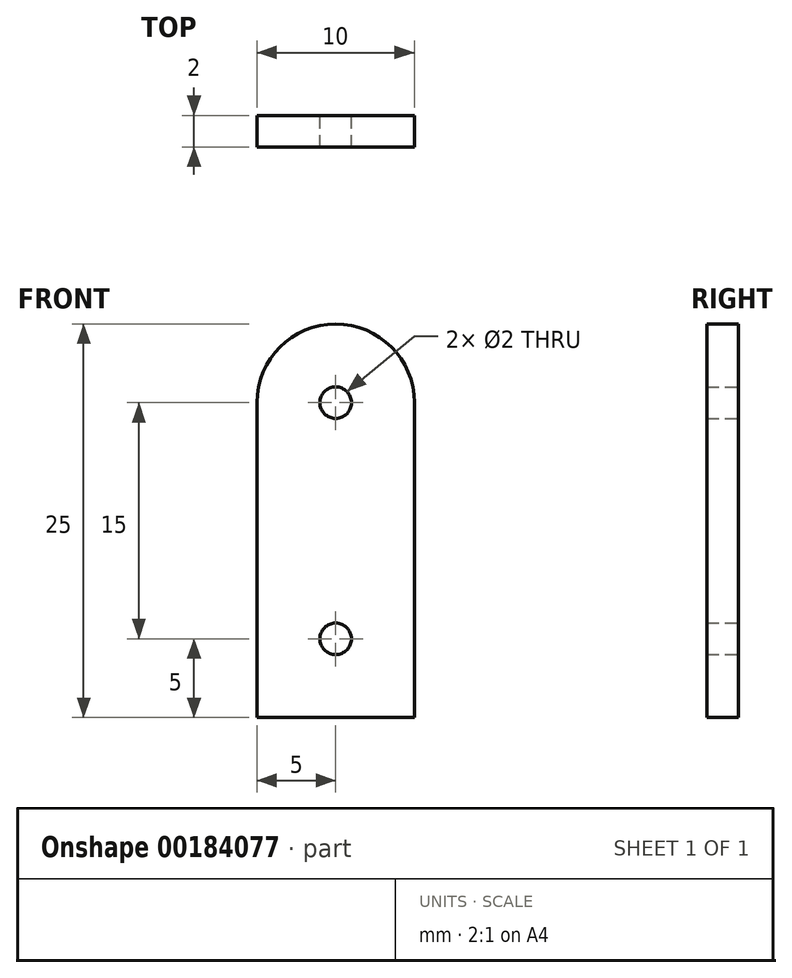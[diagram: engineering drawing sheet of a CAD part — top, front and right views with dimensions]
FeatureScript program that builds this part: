
annotation { "Feature Type Name" : "Feature", "Feature Type Description" : "" }
export const myFeature = defineFeature(function(context is Context, id is Id, definition is map)
    precondition{}
    {
        {
            var Q0;
            Q0=qCreatedBy(makeId("Front.planeOp"),FACE);
            var sketch = newSketch(context, id + "F0", { "sketchPlane" : qUnion([Q0])});
            skLineSegment(sketch, "E0.bottom", {"start": v(0, 0) * mm, "end": v(10, 0) * mm});
            skLineSegment(sketch, "E0.left", {"start": v(0, 0) * mm, "end": v(0, 20) * mm});
            skLineSegment(sketch, "E0.right", {"start": v(10, 0) * mm, "end": v(10, 20) * mm});
            skArc(sketch, "E1", {"start": v(10, 20) * mm, "mid": v(5, 25) * mm, "end": v(0, 20) * mm});
            skCircle(sketch, "E2", {"center": v(5, 20) * mm, "radius": 1 * mm});
            skCircle(sketch, "E3", {"center": v(5, 5) * mm, "radius": 1 * mm});
            skSolve(sketch);
        }
        {
            var Q0;
            Q0 = qSketchRegion(id + "F0", true);
            extrude(context, id + "F1", {"entities" : qUnion([Q0]), "depth" : 2 * mm});
        }
    });
